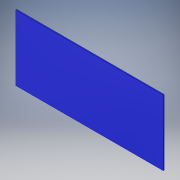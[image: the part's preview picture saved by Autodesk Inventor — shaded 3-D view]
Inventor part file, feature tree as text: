
AUTODESK INVENTOR PART (.ipt)
format: ipt  version: 2017 (Build 210142000, 142)  size: 89,088 bytes
history: native  units: in
note: dims shown in document units (in); Inventor stores cm internally (conversion verified against a paired STEP export)
features: extrude x1, sketch x1
ambient origin geometry x8: Origin, YZ Plane, XZ Plane, XY Plane, X Axis, Y Axis, Z Axis, Center Point
bodies: Solid1 (feature_tree)
feature tree (2):
  extrude  "Extrusion1"  Depth=7.875in
  sketch  "Sketch1"  dims[d1=17.75in d2=7.875in d3=17.75in d4=0.125in d5=0.0in]
